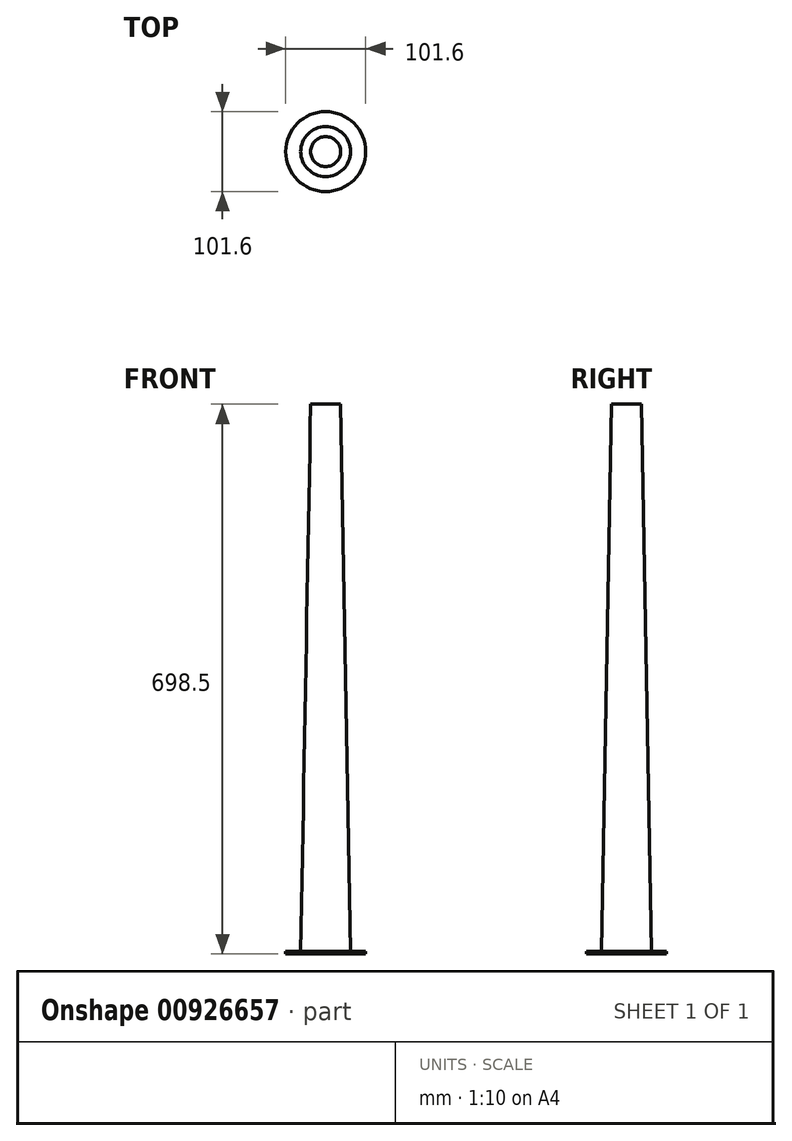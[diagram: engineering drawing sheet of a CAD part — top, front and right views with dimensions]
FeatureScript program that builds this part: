
annotation { "Feature Type Name" : "Feature", "Feature Type Description" : "" }
export const myFeature = defineFeature(function(context is Context, id is Id, definition is map)
    precondition{}
    {
        {
            var Q0;
            Q0=qCreatedBy(makeId("Front.planeOp"),FACE);
            var sketch = newSketch(context, id + "F0", { "sketchPlane" : qUnion([Q0])});
            skLineSegment(sketch, "E0", {"start": v(0, 698.5) * mm, "end": v(19.05, 698.5) * mm});
            skLineSegment(sketch, "E1", {"start": v(19.05, 698.5) * mm, "end": v(31.75, 0) * mm});
            skLineSegment(sketch, "E2", {"start": v(31.75, 0) * mm, "end": v(0, 0) * mm});
            skLineSegment(sketch, "E3", {"start": v(0, 0) * mm, "end": v(0, 698.5) * mm});
            skSolve(sketch);
        }
        {
            var Q0;
            Q0=makeQuery(id+"F0.imprint","IMPRINT",FACE,{"disambiguationData":[TD([[makeQuery(id+"F0.imprint","IMPRINT",EDGE,{"derivedFrom":sQuery(id+"F0.wireOp",EDGE,"E0")}),-1.0]])]});
            var Q1;
            Q1=sQuery(id+"F0.wireOp",EDGE,"E3");
            revolve(context, id + "F1", {"surfaceOperationType" : NewSurfaceOperationType.NEW, "entities" : qUnion([Q0]), "axis" : qUnion([Q1]), "revolveType" : RevolveType.FULL});
        }
        {
            var Q0;
            Q0=makeQuery(id+"F1.opRevolve","SWEPT_FACE",FACE,{"disambiguationData":[OSD([sQuery(id+"F0.wireOp",EDGE,"E2")])]});
            var sketch = newSketch(context, id + "F2", { "sketchPlane" : qUnion([Q0])});
            skCircle(sketch, "E4", {"center": v(0, 0) * mm, "radius": 50.8 * mm});
            skSolve(sketch);
        }
        {
            var Q0;
            Q0=makeQuery(id+"F2.imprint","IMPRINT",FACE,{"disambiguationData":[TD([[makeQuery(id+"F2.imprint","IMPRINT",EDGE,{"derivedFrom":sQuery(id+"F2.wireOp",EDGE,"E4")}),1.0]])]});
            var Q1;
            Q1=makeQuery(id+"F2.imprint","IMPRINT",FACE,{"disambiguationData":[TD([[makeQuery(id+"F2.imprint","IMPRINT",EDGE,{"derivedFrom":makeQuery(id+"F1.opRevolve","SWEPT_EDGE",EDGE,{"disambiguationData":[OSD([sQuery(id+"F0.wireOp",EDGE,"E1"),sQuery(id+"F0.wireOp",EDGE,"E2")])]})}),1.0]])]});
            extrude(context, id + "F3", {"entities" : qUnion([Q0, Q1]), "operationType" : NewBodyOperationType.ADD, "depth" : -3.17 * mm, "offsetDistance" : 25.4 * mm});
        }
    });
